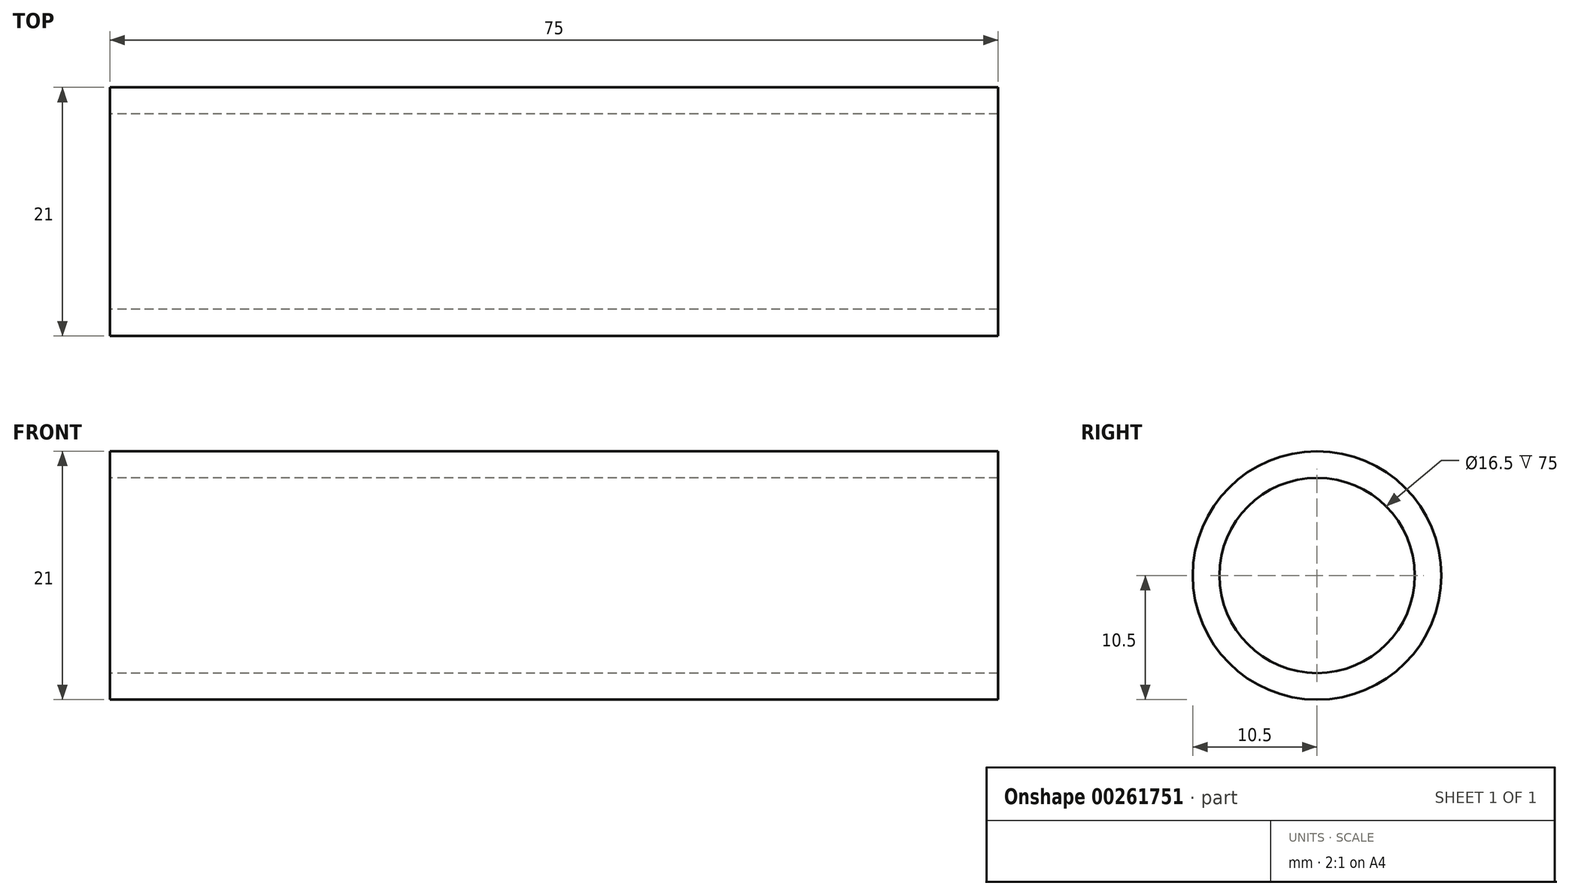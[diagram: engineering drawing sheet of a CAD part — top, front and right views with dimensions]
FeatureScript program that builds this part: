
annotation { "Feature Type Name" : "Feature", "Feature Type Description" : "" }
export const myFeature = defineFeature(function(context is Context, id is Id, definition is map)
    precondition{}
    {
        {
            var Q0;
            Q0=qCreatedBy(makeId("Front.planeOp"),FACE);
            var sketch = newSketch(context, id + "F0", { "sketchPlane" : qUnion([Q0])});
            skLineSegment(sketch, "E0", {"start": v(-49, 0) * mm, "end": v(45.22, 0) * mm, "construction": true});
            skLineSegment(sketch, "E1", {"start": v(0, 8.25) * mm, "end": v(37.5, 8.25) * mm});
            skLineSegment(sketch, "E2", {"start": v(37.5, 8.25) * mm, "end": v(37.5, 10.5) * mm});
            skLineSegment(sketch, "E3", {"start": v(37.5, 10.5) * mm, "end": v(0, 10.5) * mm});
            skLineSegment(sketch, "E4.MirrorCS", {"start": v(0, 8.25) * mm, "end": v(-37.5, 8.25) * mm});
            skLineSegment(sketch, "E5.MirrorCS", {"start": v(-37.5, 10.5) * mm, "end": v(0, 10.5) * mm});
            skLineSegment(sketch, "E6.MirrorCS", {"start": v(-37.5, 8.25) * mm, "end": v(-37.5, 10.5) * mm});
            skSolve(sketch);
        }
        {
            var Q0;
            Q0=makeQuery(id+"F0.imprint","IMPRINT",FACE,{"disambiguationData":[TD([[makeQuery(id+"F0.imprint","IMPRINT",EDGE,{"derivedFrom":sQuery(id+"F0.wireOp",EDGE,"E1")}),1.0]])]});
            var Q1;
            Q1=sQuery(id+"F0.wireOp",EDGE,"E0");
            revolve(context, id + "F1", {"entities" : qUnion([Q0]), "axis" : qUnion([Q1]), "revolveType" : RevolveType.FULL});
        }
    });
